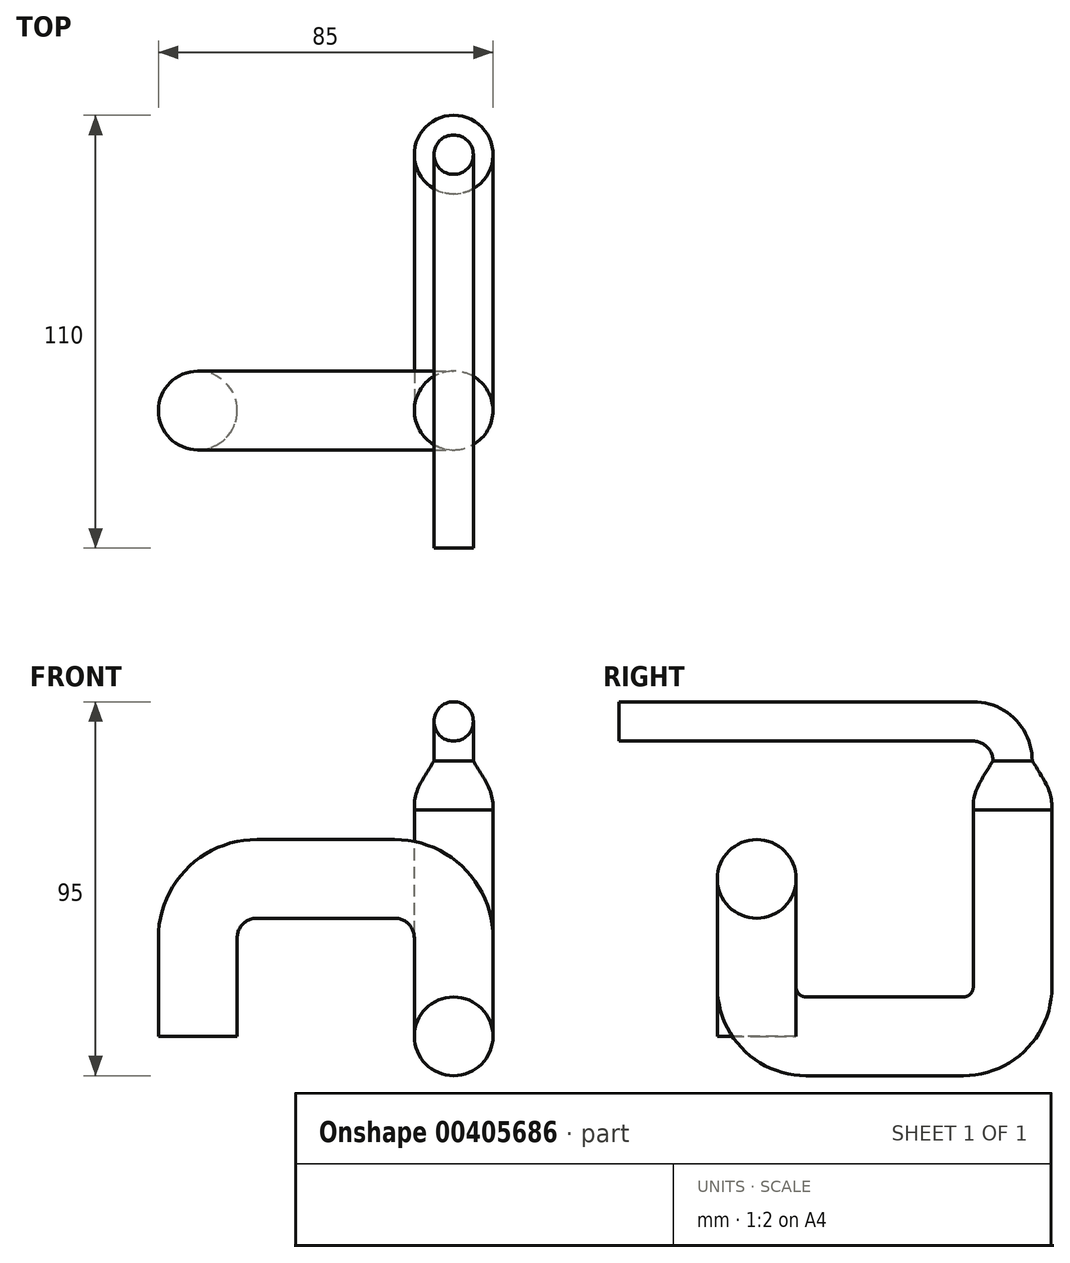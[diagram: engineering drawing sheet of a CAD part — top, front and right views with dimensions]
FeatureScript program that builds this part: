
annotation { "Feature Type Name" : "Feature", "Feature Type Description" : "" }
export const myFeature = defineFeature(function(context is Context, id is Id, definition is map)
    precondition{}
    {
        {
            var Q0;
            Q0=qCreatedBy(makeId("Top.planeOp"),FACE);
            var sketch = newSketch(context, id + "F0", { "sketchPlane" : qUnion([Q0])});
            skCircle(sketch, "E0", {"center": v(0, 0) * mm, "radius": 10 * mm});
            skLineSegment(sketch, "E1", {"start": v(0, 0) * mm, "end": v(65, 0) * mm});
            skPoint(sketch, "E2", {"position": v(65, 12.5) * mm});
            skSolve(sketch);
        }
        {
            var Q0;
            Q0=qCreatedBy(makeId("Front.planeOp"),FACE);
            var sketch = newSketch(context, id + "F1", { "sketchPlane" : qUnion([Q0])});
            skLineSegment(sketch, "E3.0", {"start": v(0, 0) * mm, "end": v(0, 25) * mm});
            skArc(sketch, "E4.0", {"start": v(15, 40) * mm, "mid": v(4.4, 35.6) * mm, "end": v(0, 25) * mm});
            skLineSegment(sketch, "E5.0", {"start": v(45, 40) * mm, "end": v(15, 40) * mm});
            skLineSegment(sketch, "E5.1", {"start": v(50, 40) * mm, "end": v(45, 40) * mm});
            skArc(sketch, "E5.2", {"start": v(50, 40) * mm, "mid": v(60.6, 35.6) * mm, "end": v(65, 25) * mm});
            skLineSegment(sketch, "E5.3", {"start": v(65, 25) * mm, "end": v(65, 12.5) * mm});
            skPoint(sketch, "E6", {"position": v(65, 12.5) * mm});
            skPoint(sketch, "E7.orphan", {"position": v(65, 0) * mm});
            skSolve(sketch);
        }
        {
            var Q0;
            Q0=makeQuery(id+"F0.imprint","IMPRINT",FACE,{"disambiguationData":[TD([[makeQuery(id+"F0.imprint","IMPRINT",EDGE,{"derivedFrom":sQuery(id+"F0.wireOp",EDGE,"E0")}),1.0]])]});
            var Q1;
            Q1=sQuery(id+"F1.wireOp",EDGE,"E3.0");
            var Q2;
            Q2=sQuery(id+"F1.wireOp",EDGE,"E4.0");
            var Q3;
            Q3=sQuery(id+"F1.wireOp",EDGE,"E5.0");
            var Q4;
            Q4=sQuery(id+"F1.wireOp",EDGE,"E5.2");
            var Q5;
            Q5=sQuery(id+"F1.wireOp",EDGE,"E5.3");
            var Q6;
            Q6=sQuery(id+"F1.wireOp",EDGE,"E5.1");
            var Q7;
            Q7=sQuery(id+"F0.wireOp",EDGE,"3Ayk6dHC-uAVS-XBJq-wXRU-8m2HeRQmatkH");
            var Q8;
            Q8=qConstructionFilter(qBodyType(qCreatedBy(id+"F4",EDGE),BodyType.WIRE),ConstructionObject.NO);
            sweep(context, id + "F2", {"profiles" : qUnion([Q0]), "path" : qUnion([Q1, Q2, Q3, Q4, Q5, Q6, Q7, Q8])});
        }
        {
            var Q0;
            Q0=qCreatedBy(makeId("Right.planeOp"),FACE);
            var Q1;
            Q1=qBodyType(qCreatedBy(id+"F4",EDGE),BodyType.WIRE);
            cPlane(context, id + "F3", {"entities" : qUnion([Q0, Q1]), "cplaneType" : CPlaneType.OFFSET, "offset" : 65 * mm, "width" : 150 * mm, "height" : 150 * mm});
        }
        {
            var Q0;
            Q0=qCreatedBy(id+"F3.planeOp",FACE);
            var sketch = newSketch(context, id + "F4", { "sketchPlane" : qUnion([Q0])});
            skPoint(sketch, "E8.0", {"position": v(0, 12.5) * mm});
            skPoint(sketch, "E9.0", {"position": v(12.5, 0) * mm});
            skArc(sketch, "E10", {"start": v(12.5, 0) * mm, "mid": v(3.66, 3.66) * mm, "end": v(0, 12.5) * mm});
            skLineSegment(sketch, "E11", {"start": v(12.5, 0) * mm, "end": v(52.5, 0) * mm});
            skArc(sketch, "E12", {"start": v(52.5, 0) * mm, "mid": v(61.34, 3.66) * mm, "end": v(65, 12.5) * mm});
            skLineSegment(sketch, "E13", {"start": v(65, 12.5) * mm, "end": v(65, 57.5) * mm});
            skLineSegment(sketch, "E14", {"start": v(65, 0) * mm, "end": v(65, 70) * mm});
            skPoint(sketch, "E14.endSnap0", {"position": v(65, 35) * mm});
            skArc(sketch, "E15", {"start": v(65, 70) * mm, "mid": v(62.07, 77.07) * mm, "end": v(55, 80) * mm});
            skLineSegment(sketch, "E16", {"start": v(55, 80) * mm, "end": v(-35, 80) * mm});
            skSolve(sketch);
        }
        {
            var Q0;
            Q0=qCreatedBy(makeId("Front.planeOp"),FACE);
            cPlane(context, id + "F5", {"entities" : qUnion([Q0]), "cplaneType" : CPlaneType.OFFSET, "offset" : 52.5 * mm, "oppositeDirection" : true, "width" : 150 * mm, "height" : 150 * mm});
        }
        {
            var Q0;
            Q0=qCreatedBy(id+"F5.planeOp",FACE);
            var sketch = newSketch(context, id + "F6", { "sketchPlane" : qUnion([Q0])});
            skPoint(sketch, "E17.0", {"position": v(65, 0) * mm});
            skCircle(sketch, "E18", {"center": v(65, 0) * mm, "radius": 10 * mm});
            skSolve(sketch);
        }
        {
            var Q0;
            Q0=makeQuery(id+"F6.imprint","IMPRINT",FACE,{"disambiguationData":[TD([[makeQuery(id+"F6.imprint","IMPRINT",EDGE,{"derivedFrom":sQuery(id+"F6.wireOp",EDGE,"E18")}),1.0]])]});
            var Q1;
            Q1=sQuery(id+"F4.wireOp",EDGE,"E11");
            var Q2;
            Q2=sQuery(id+"F4.wireOp",EDGE,"E10");
            sweep(context, id + "F7", {"operationType" : NewBodyOperationType.ADD, "profiles" : qUnion([Q0]), "path" : qUnion([Q1, Q2])});
        }
        {
            var Q0;
            Q0=makeQuery(id+"F7.opSweep","CAP_FACE",FACE,{"disambiguationData":[OSD([sQuery(id+"F4.wireOp",VERTEX,"E11.end"),sQuery(id+"F6.wireOp",EDGE,"E18")])],"isStart":true});
            var Q1;
            Q1=sQuery(id+"F4.wireOp",EDGE,"E12");
            var Q2;
            Q2=sQuery(id+"F4.wireOp",EDGE,"E13");
            sweep(context, id + "F8", {"operationType" : NewBodyOperationType.ADD, "profiles" : qUnion([Q0]), "path" : qUnion([Q1, Q2])});
        }
        {
            var Q0;
            Q0=qCreatedBy(makeId("Top.planeOp"),FACE);
            cPlane(context, id + "F9", {"entities" : qUnion([Q0]), "cplaneType" : CPlaneType.OFFSET, "offset" : 70 * mm, "width" : 150 * mm, "height" : 150 * mm});
        }
        {
            var Q0;
            Q0=qCreatedBy(id+"F9.planeOp",FACE);
            var sketch = newSketch(context, id + "F10", { "sketchPlane" : qUnion([Q0])});
            skPoint(sketch, "E19.0", {"position": v(65, 65) * mm});
            skCircle(sketch, "E20", {"center": v(65, 65) * mm, "radius": 5 * mm});
            skSolve(sketch);
        }
        {
            var Q0;
            Q0=makeQuery(id+"F10.imprint","IMPRINT",FACE,{"disambiguationData":[TD([[makeQuery(id+"F10.imprint","IMPRINT",EDGE,{"derivedFrom":sQuery(id+"F10.wireOp",EDGE,"E20")}),1.0]])]});
            var Q1;
            Q1=sQuery(id+"F4.wireOp",EDGE,"E15");
            var Q2;
            Q2=sQuery(id+"F4.wireOp",EDGE,"E16");
            sweep(context, id + "F11", {"profiles" : qUnion([Q0]), "path" : qUnion([Q1, Q2])});
        }
        {
            var Q0;
            Q0=makeQuery(id+"F8.opSweep","CAP_FACE",FACE,{"disambiguationData":[OSD([sQuery(id+"F4.wireOp",VERTEX,"E11.end"),sQuery(id+"F4.wireOp",VERTEX,"E13.end"),sQuery(id+"F6.wireOp",EDGE,"E18")])],"isStart":false});
            var Q1;
            Q1=makeQuery(id+"F11.opSweep","CAP_FACE",FACE,{"disambiguationData":[OSD([sQuery(id+"F4.wireOp",VERTEX,"E15.start"),sQuery(id+"F10.wireOp",EDGE,"E20")])],"isStart":true});
            loft(context, id + "F12", {"startCondition" : LoftEndDerivativeType.MATCH_CURVATURE, "startMagnitude" : 1, "endCondition" : LoftEndDerivativeType.MATCH_CURVATURE, "endMagnitude" : 0, "sheetProfilesArray" : [{ "sheetProfileEntities" : qUnion([Q0]) }, { "sheetProfileEntities" : qUnion([Q1]) }]});
        }
    });
